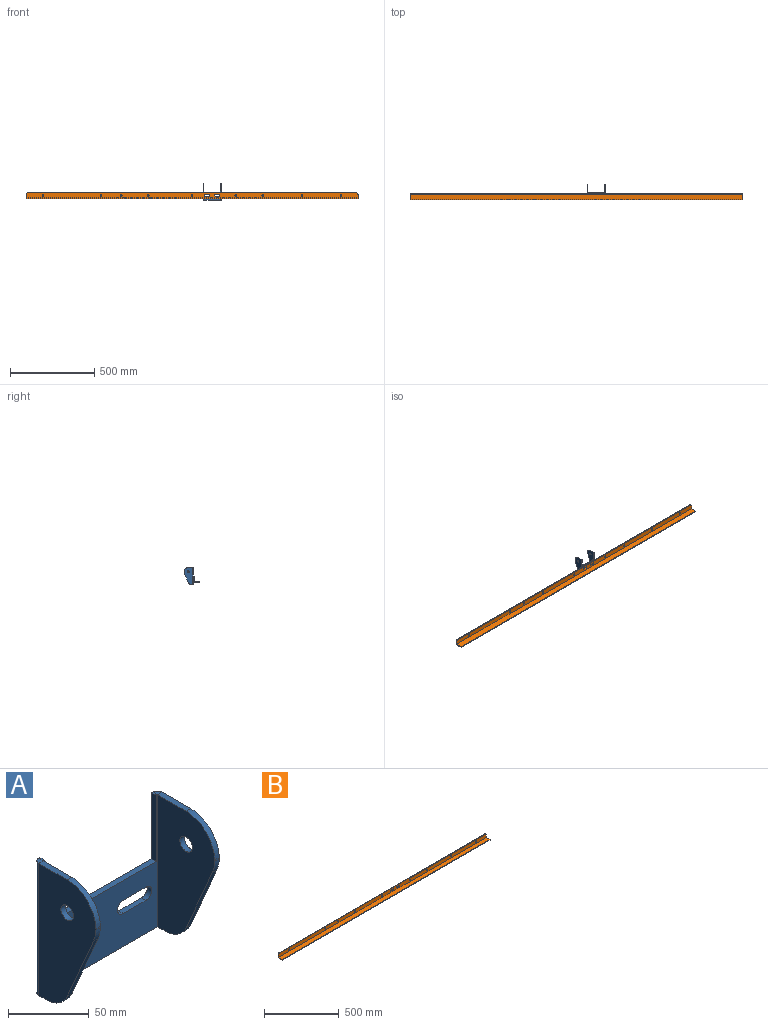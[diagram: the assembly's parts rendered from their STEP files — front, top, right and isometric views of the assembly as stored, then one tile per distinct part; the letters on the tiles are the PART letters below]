
ASSEMBLY  parts=2 mates=1
PART A: 44 faces, bbox 108x54x100 mm
  f0: plane 20x4mm, normal (0,0,1), area 80mm2, adj f1,f13,f14,f15
  f1: cylinder r=5mm len=10mm, axis (0,1,0), area 62.8mm2, adj f0,f2,f14,f15
  f2: plane 20x4mm, normal (0,0,-1), area 80mm2, adj f1,f13,f14,f15
  f3: plane 20x4mm, normal (0,0,1), area 80mm2, adj f4,f12,f14,f15
  f4: cylinder r=5mm len=10mm, axis (0,1,0), area 62.8mm2, adj f3,f5,f14,f15
  f5: plane 20x4mm, normal (0,0,-1), area 80mm2, adj f4,f12,f14,f15
  f6: plane 97.98x4mm, normal (0,0,1), area 391.9mm2, adj f7,f11,f14,f15
  f7: plane 50x4mm, normal (-1,0,0), area 200mm2, adj f6,f8,f14,f15
  f8: plane 4x1mm, normal (0,0,1), area 4mm2, adj f7,f14,f15,f40
  f9: plane 99.98x4mm, normal (0,0,-1), area 399.9mm2, adj f14,f15,f27,f41
  f10: plane 4x1mm, normal (0,0,1), area 4mm2, adj f11,f14,f15,f26
  f11: plane 50x4mm, normal (1,0,0), area 200mm2, adj f6,f10,f14,f15
  f12: cylinder r=5mm len=10mm, axis (0,1,0), area 62.8mm2, adj f3,f5,f14,f15
  f13: cylinder r=5mm len=10mm, axis (0,1,0), area 62.8mm2, adj f0,f2,f14,f15
  f14: plane 100x99.98mm, normal (0,1,0), area 4541.9mm2, adj f0,f1,f2,f3,f4,f5,f6,f7
  f15: plane 100x99.98mm, normal (0,-1,0), area 4541.9mm2, adj f0,f1,f2,f3,f4,f5,f6,f7
  f16: plane 4x1mm, normal (0,-1,0), area 4mm2, adj f17,f22,f23,f24
  f17: cylinder r=25mm len=25mm, axis (-1,0,0), area 155.1mm2, adj f16,f18,f23,f24
  f18: plane 25x4mm, normal (0,0,1), area 100mm2, adj f17,f23,f24,f26
  f19: plane 6.82x4mm, normal (0,0,-1), area 27.3mm2, adj f23,f24,f25,f27
  f20: plane 53.03x22.77mm, normal (0,-0.92,-0.39), area 230.8mm2, adj f22,f23,f24,f25
  f21: cylinder r=5.5mm len=11mm, axis (-1,0,0), area 138.2mm2, adj f23,f24
  f22: cylinder r=25mm len=9.36mm, axis (-1,0,0), area 38.6mm2, adj f16,f20,f23,f24
  f23: plane 100x49.99mm, normal (-1,0,0), area 3690.3mm2, adj f16,f17,f18,f19,f20,f21,f22,f25
  f24: plane 100x49.99mm, normal (1,0,0), area 3690.3mm2, adj f16,f17,f18,f19,f20,f21,f22,f25
  f25: cylinder r=20mm len=18.38mm, axis (1,0,0), area 93.2mm2, adj f19,f20,f23,f24
  f26: plane 4.01x4.01mm, normal (0,0,1), area 12.6mm2, adj f10,f18,f28,f29
  f27: plane 4.01x4.01mm, normal (0,0,-1), area 12.6mm2, adj f9,f19,f28,f29
  f28: cylinder r=4.01mm len=100mm, axis (0,0,1), area 629.9mm2, adj f14,f23,f26,f27
  f29: cylinder r=0.01mm len=100mm, axis (0,0,1), area 1.6mm2, adj f15,f24,f26,f27
  f30: plane 53.03x22.78mm, normal (0,-0.92,-0.39), area 230.8mm2, adj f36,f37,f38,f39
  f31: plane 6.81x4mm, normal (0,0,-1), area 27.3mm2, adj f37,f38,f39,f41
  f32: plane 25x4mm, normal (0,0,1), area 100mm2, adj f33,f37,f38,f40
  f33: cylinder r=25mm len=25mm, axis (1,0,0), area 155.1mm2, adj f32,f34,f37,f38
  f34: plane 4x1mm, normal (0,-1,0), area 4mm2, adj f33,f36,f37,f38
  f35: cylinder r=5.5mm len=11mm, axis (1,0,0), area 138.2mm2, adj f37,f38
  f36: cylinder r=25mm len=9.37mm, axis (1,0,0), area 38.6mm2, adj f30,f34,f37,f38
  f37: plane 100x49.99mm, normal (1,0,0), area 3690mm2, adj f30,f31,f32,f33,f34,f35,f36,f39
  f38: plane 100x49.99mm, normal (-1,0,0), area 3690mm2, adj f30,f31,f32,f33,f34,f35,f36,f39
  f39: cylinder r=20mm len=18.38mm, axis (-1,0,0), area 93.2mm2, adj f30,f31,f37,f38
  f40: plane 4.01x4.01mm, normal (0,0,1), area 12.6mm2, adj f8,f32,f42,f43
  f41: plane 4.01x4.01mm, normal (0,0,-1), area 12.6mm2, adj f9,f31,f42,f43
  f42: cylinder r=4.01mm len=100mm, axis (0,0,1), area 629.9mm2, adj f14,f37,f40,f41
  f43: cylinder r=0.01mm len=100mm, axis (0,0,1), area 1.6mm2, adj f15,f38,f40,f41
PART B: 33 faces, bbox 1970x40x35 mm
  f0: plane 19.99x5mm, normal (-1,0,0), area 100mm2, adj f20,f21,f22,f29
  f1: plane 1950x5mm, normal (0,0,1), area 9750mm2, adj f20,f21,f22,f23
  f2: plane 19.99x5mm, normal (1,0,0), area 100mm2, adj f20,f21,f23,f30
  f3: plane 20x5mm, normal (0,0,1), area 100mm2, adj f4,f14,f20,f21
  f4: cylinder r=5mm len=10mm, axis (0,1,0), area 78.5mm2, adj f3,f5,f20,f21
  f5: plane 20x5mm, normal (0,0,-1), area 100mm2, adj f4,f14,f20,f21
  f6: plane 20x5mm, normal (0,0,1), area 100mm2, adj f7,f12,f20,f21
  f7: cylinder r=5mm len=10mm, axis (0,1,0), area 78.5mm2, adj f6,f8,f20,f21
  f8: plane 20x5mm, normal (0,0,-1), area 100mm2, adj f7,f12,f20,f21
  f9: cylinder r=5mm len=10mm, axis (0,1,0), area 157.1mm2, adj f20,f21
  f10: cylinder r=5mm len=10mm, axis (0,1,0), area 157.1mm2, adj f20,f21
  f11: cylinder r=5mm len=10mm, axis (0,1,0), area 157.1mm2, adj f20,f21
  f12: cylinder r=5mm len=10mm, axis (0,1,0), area 78.5mm2, adj f6,f8,f20,f21
  f13: cylinder r=5mm len=10mm, axis (0,1,0), area 157.1mm2, adj f20,f21
  f14: cylinder r=5mm len=10mm, axis (0,1,0), area 78.5mm2, adj f3,f5,f20,f21
  f15: cylinder r=5mm len=10mm, axis (0,1,0), area 157.1mm2, adj f20,f21
  f16: cylinder r=5mm len=10mm, axis (0,1,0), area 157.1mm2, adj f20,f21
  f17: cylinder r=5mm len=10mm, axis (0,1,0), area 157.1mm2, adj f20,f21
  f18: cylinder r=5mm len=10mm, axis (0,1,0), area 157.1mm2, adj f20,f21
  f19: cylinder r=5mm len=10mm, axis (0,1,0), area 157.1mm2, adj f20,f21
  f20: plane 1970x29.99mm, normal (0,1,0), area 57773.4mm2, adj f0,f1,f2,f3,f4,f5,f6,f7
  f21: plane 1970x29.99mm, normal (0,-1,0), area 57773.4mm2, adj f0,f1,f2,f3,f4,f5,f6,f7
  f22: cylinder r=10mm len=10mm, axis (0,1,0), area 78.5mm2, adj f0,f1,f20,f21
  f23: cylinder r=10mm len=10mm, axis (0,-1,0), area 78.5mm2, adj f1,f2,f20,f21
  f24: plane 1970x5mm, normal (0,-1,0), area 9850mm2, adj f25,f26,f27,f28
  f25: plane 34.99x5mm, normal (-1,0,0), area 175mm2, adj f24,f27,f28,f29
  f26: plane 34.99x5mm, normal (1,0,0), area 175mm2, adj f24,f27,f28,f30
  f27: plane 1970x34.99mm, normal (0,0,-1), area 68930.3mm2, adj f24,f25,f26,f31
  f28: plane 1970x34.99mm, normal (0,0,1), area 68930.3mm2, adj f24,f25,f26,f32
  f29: plane 5.01x5.01mm, normal (-1,0,0), area 19.7mm2, adj f0,f25,f31,f32
  f30: plane 5.01x5.01mm, normal (1,0,0), area 19.7mm2, adj f2,f26,f31,f32
  f31: cylinder r=5.01mm len=1970mm, axis (-1,0,0), area 15503.3mm2, adj f20,f27,f29,f30
  f32: cylinder r=0.01mm len=1970mm, axis (-1,0,0), area 30.9mm2, adj f21,f28,f29,f30
PLACE A rot(axis=(0,0,1),180deg) t=(-39.16,365.06,-149.6)mm
PLACE B t=(-1194.16,356.06,-139.6)mm
MATE fastened B.f20 <-> A.f14  axis (0,1,0) through (-59.16,361.06,-119.6)mm
